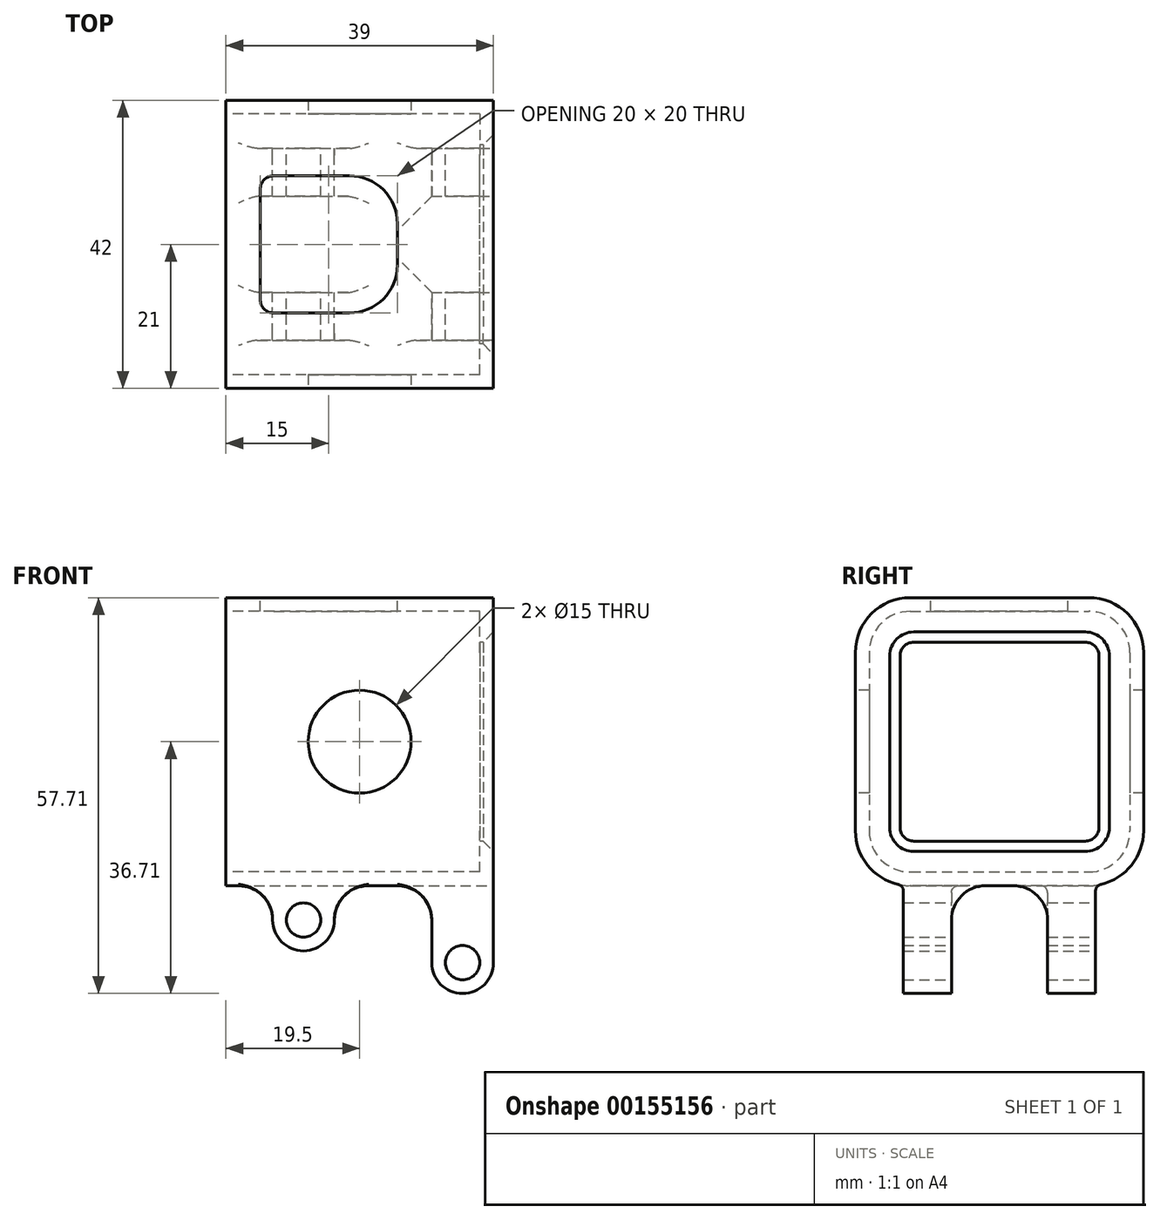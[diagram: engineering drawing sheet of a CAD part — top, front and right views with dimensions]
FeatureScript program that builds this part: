
annotation { "Feature Type Name" : "Feature", "Feature Type Description" : "" }
export const myFeature = defineFeature(function(context is Context, id is Id, definition is map)
    precondition{}
    {
        {
            var Q0;
            Q0=qCreatedBy(makeId("Right.planeOp"),FACE);
            var sketch = newSketch(context, id + "F0", { "sketchPlane" : qUnion([Q0])});
            skLineSegment(sketch, "E0.bottom", {"start": v(-13, 21) * mm, "end": v(13, 21) * mm});
            skLineSegment(sketch, "E0.top", {"start": v(-13, -21) * mm, "end": v(13, -21) * mm});
            skLineSegment(sketch, "E0.left", {"start": v(-21, 13) * mm, "end": v(-21, -13) * mm});
            skLineSegment(sketch, "E0.right", {"start": v(21, 13) * mm, "end": v(21, -13) * mm});
            skLineSegment(sketch, "E1.bottom", {"start": v(-13, 19) * mm, "end": v(13, 19) * mm});
            skLineSegment(sketch, "E1.top", {"start": v(-13, -19) * mm, "end": v(13, -19) * mm});
            skLineSegment(sketch, "E1.left", {"start": v(-19, 13) * mm, "end": v(-19, -13) * mm});
            skLineSegment(sketch, "E1.right", {"start": v(19, 13) * mm, "end": v(19, -13) * mm});
            skPoint(sketch, "E2.visualSharp", {"position": v(-19, 19) * mm});
            skArc(sketch, "E2.filletArc", {"start": v(-13, 19) * mm, "mid": v(-17.24, 17.24) * mm, "end": v(-19, 13) * mm});
            skPoint(sketch, "E3.visualSharp", {"position": v(19, 19) * mm});
            skArc(sketch, "E3.filletArc", {"start": v(19, 13) * mm, "mid": v(17.24, 17.24) * mm, "end": v(13, 19) * mm});
            skPoint(sketch, "E4.visualSharp", {"position": v(19, -19) * mm});
            skArc(sketch, "E4.filletArc", {"start": v(13, -19) * mm, "mid": v(17.24, -17.24) * mm, "end": v(19, -13) * mm});
            skPoint(sketch, "E5.visualSharp", {"position": v(-19, -19) * mm});
            skArc(sketch, "E5.filletArc", {"start": v(-19, -13) * mm, "mid": v(-17.24, -17.24) * mm, "end": v(-13, -19) * mm});
            skPoint(sketch, "E6.visualSharp", {"position": v(-21, -21) * mm});
            skArc(sketch, "E6.filletArc", {"start": v(-21, -13) * mm, "mid": v(-18.66, -18.66) * mm, "end": v(-13, -21) * mm});
            skPoint(sketch, "E7.visualSharp", {"position": v(21, -21) * mm});
            skArc(sketch, "E7.filletArc", {"start": v(13, -21) * mm, "mid": v(18.66, -18.66) * mm, "end": v(21, -13) * mm});
            skPoint(sketch, "E8.visualSharp", {"position": v(21, 21) * mm});
            skArc(sketch, "E8.filletArc", {"start": v(21, 13) * mm, "mid": v(18.66, 18.66) * mm, "end": v(13, 21) * mm});
            skPoint(sketch, "E9.visualSharp", {"position": v(-21, 21) * mm});
            skArc(sketch, "E9.filletArc", {"start": v(-13, 21) * mm, "mid": v(-18.66, 18.66) * mm, "end": v(-21, 13) * mm});
            skSolve(sketch);
        }
        {
            var Q0;
            Q0 = qSketchRegion(id + "F0", true);
            extrude(context, id + "F1", {"entities" : qUnion([Q0]), "endBound" : BoundingType.SYMMETRIC, "depth" : 37 * mm});
        }
        {
            var Q0;
            Q0=makeQuery(id+"F1.opExtrude","CAP_FACE",FACE,{"disambiguationData":[OSD([sQuery(id+"F0.wireOp",EDGE,"E0.bottom"),sQuery(id+"F0.wireOp",EDGE,"E0.top"),sQuery(id+"F0.wireOp",EDGE,"E0.left"),sQuery(id+"F0.wireOp",EDGE,"E0.right"),sQuery(id+"F0.wireOp",EDGE,"E1.bottom"),sQuery(id+"F0.wireOp",EDGE,"E1.top"),sQuery(id+"F0.wireOp",EDGE,"E1.left"),sQuery(id+"F0.wireOp",EDGE,"E1.right"),sQuery(id+"F0.wireOp",EDGE,"E2.filletArc"),sQuery(id+"F0.wireOp",EDGE,"E3.filletArc"),sQuery(id+"F0.wireOp",EDGE,"E4.filletArc"),sQuery(id+"F0.wireOp",EDGE,"E5.filletArc"),sQuery(id+"F0.wireOp",EDGE,"E6.filletArc"),sQuery(id+"F0.wireOp",EDGE,"E7.filletArc"),sQuery(id+"F0.wireOp",EDGE,"E8.filletArc"),sQuery(id+"F0.wireOp",EDGE,"E9.filletArc")])],"isStart":false});
            var sketch = newSketch(context, id + "F2", { "sketchPlane" : qUnion([Q0])});
            skLineSegment(sketch, "E10.bottom", {"start": v(-12.5, 14.5) * mm, "end": v(12.5, 14.5) * mm});
            skLineSegment(sketch, "E10.top", {"start": v(-12.5, -14.5) * mm, "end": v(12.5, -14.5) * mm});
            skLineSegment(sketch, "E10.left", {"start": v(-14.5, 12.5) * mm, "end": v(-14.5, -12.5) * mm});
            skLineSegment(sketch, "E10.right", {"start": v(14.5, 12.5) * mm, "end": v(14.5, -12.5) * mm});
            skLineSegment(sketch, "E11.bottom", {"start": v(-13, 21) * mm, "end": v(13, 21) * mm});
            skLineSegment(sketch, "E11.top", {"start": v(-13, -21) * mm, "end": v(13, -21) * mm});
            skLineSegment(sketch, "E11.left", {"start": v(-21, 13) * mm, "end": v(-21, -13) * mm});
            skLineSegment(sketch, "E11.right", {"start": v(21, 13) * mm, "end": v(21, -13) * mm});
            skPoint(sketch, "E12.visualSharp", {"position": v(-21, 21) * mm});
            skArc(sketch, "E12.filletArc", {"start": v(-13, 21) * mm, "mid": v(-18.66, 18.66) * mm, "end": v(-21, 13) * mm});
            skPoint(sketch, "E13.visualSharp", {"position": v(-21, -21) * mm});
            skArc(sketch, "E13.filletArc", {"start": v(-21, -13) * mm, "mid": v(-18.66, -18.66) * mm, "end": v(-13, -21) * mm});
            skPoint(sketch, "E14.visualSharp", {"position": v(21, -21) * mm});
            skArc(sketch, "E14.filletArc", {"start": v(13, -21) * mm, "mid": v(18.66, -18.66) * mm, "end": v(21, -13) * mm});
            skPoint(sketch, "E15.visualSharp", {"position": v(21, 21) * mm});
            skArc(sketch, "E15.filletArc", {"start": v(21, 13) * mm, "mid": v(18.66, 18.66) * mm, "end": v(13, 21) * mm});
            skPoint(sketch, "E16.visualSharp", {"position": v(-14.5, 14.5) * mm});
            skArc(sketch, "E16.filletArc", {"start": v(-12.5, 14.5) * mm, "mid": v(-13.91, 13.91) * mm, "end": v(-14.5, 12.5) * mm});
            skPoint(sketch, "E17.visualSharp", {"position": v(-14.5, -14.5) * mm});
            skArc(sketch, "E17.filletArc", {"start": v(-14.5, -12.5) * mm, "mid": v(-13.91, -13.91) * mm, "end": v(-12.5, -14.5) * mm});
            skPoint(sketch, "E18.visualSharp", {"position": v(14.5, -14.5) * mm});
            skArc(sketch, "E18.filletArc", {"start": v(12.5, -14.5) * mm, "mid": v(13.91, -13.91) * mm, "end": v(14.5, -12.5) * mm});
            skPoint(sketch, "E19.visualSharp", {"position": v(14.5, 14.5) * mm});
            skArc(sketch, "E19.filletArc", {"start": v(14.5, 12.5) * mm, "mid": v(13.91, 13.91) * mm, "end": v(12.5, 14.5) * mm});
            skSolve(sketch);
        }
        {
            var Q0;
            Q0 = qSketchRegion(id + "F2", true);
            extrude(context, id + "F3", {"entities" : qUnion([Q0]), "operationType" : NewBodyOperationType.ADD, "depth" : 2 * mm});
        }
        {
            var Q0;
            Q0=makeQuery(id+"F3.opExtrude","CAP_EDGE",EDGE,{"disambiguationData":[OSD([sQuery(id+"F2.wireOp",EDGE,"E10.bottom")])],"isStart":false});
            chamfer(context, id + "F4", {"entities" : qUnion([Q0]), "width" : 1.5 * mm, "tangentPropagation" : true});
        }
        {
            var Q0;
            Q0=makeQuery(id+"F3.boolean.opBoolean","MERGE",FACE,{"derivedFrom":[makeQuery(id+"F1.opExtrude","SWEPT_FACE",FACE,{"disambiguationData":[OSD([sQuery(id+"F0.wireOp",EDGE,"E0.bottom")])]}),makeQuery(id+"F3.opExtrude","SWEPT_FACE",FACE,{"disambiguationData":[OSD([sQuery(id+"F2.wireOp",EDGE,"E11.bottom")])]})]});
            var sketch = newSketch(context, id + "F5", { "sketchPlane" : qUnion([Q0])});
            skLineSegment(sketch, "E20.bottom", {"start": v(-11.5, 10) * mm, "end": v(-0.5, 10) * mm});
            skLineSegment(sketch, "E20.top", {"start": v(-11.5, -10) * mm, "end": v(-0.5, -10) * mm});
            skLineSegment(sketch, "E20.left", {"start": v(-13.5, 8) * mm, "end": v(-13.5, -8) * mm});
            skLineSegment(sketch, "E20.right", {"start": v(6.5, 3) * mm, "end": v(6.5, -3) * mm});
            skPoint(sketch, "E21.visualSharp", {"position": v(-13.5, 10) * mm});
            skArc(sketch, "E21.filletArc", {"start": v(-11.5, 10) * mm, "mid": v(-12.91, 9.41) * mm, "end": v(-13.5, 8) * mm});
            skPoint(sketch, "E22.visualSharp", {"position": v(-13.5, -10) * mm});
            skArc(sketch, "E22.filletArc", {"start": v(-13.5, -8) * mm, "mid": v(-12.91, -9.41) * mm, "end": v(-11.5, -10) * mm});
            skPoint(sketch, "E23.visualSharp", {"position": v(6.5, 10) * mm});
            skArc(sketch, "E23.filletArc", {"start": v(6.5, 3) * mm, "mid": v(4.45, 7.95) * mm, "end": v(-0.5, 10) * mm});
            skPoint(sketch, "E24.visualSharp", {"position": v(6.5, -10) * mm});
            skArc(sketch, "E24.filletArc", {"start": v(-0.5, -10) * mm, "mid": v(4.45, -7.95) * mm, "end": v(6.5, -3) * mm});
            skSolve(sketch);
        }
        {
            var Q0;
            Q0 = qSketchRegion(id + "F5", true);
            extrude(context, id + "F6", {"entities" : qUnion([Q0]), "operationType" : NewBodyOperationType.REMOVE, "oppositeDirection" : true, "depth" : 5 * mm});
        }
        {
            var Q0;
            Q0=qCreatedBy(makeId("Front.planeOp"),FACE);
            var sketch = newSketch(context, id + "F7", { "sketchPlane" : qUnion([Q0])});
            skCircle(sketch, "E25", {"center": v(16, -32.21) * mm, "radius": 2.5 * mm});
            skCircle(sketch, "E26", {"center": v(-7.18, -26) * mm, "radius": 2.5 * mm});
            skLineSegment(sketch, "E27", {"start": v(-7.18, -26) * mm, "end": v(16, -32.21) * mm, "construction": true});
            skArc(sketch, "E28", {"start": v(11.5, -32.21) * mm, "mid": v(16, -36.71) * mm, "end": v(20.5, -32.21) * mm});
            skArc(sketch, "E29", {"start": v(-11.68, -26) * mm, "mid": v(-7.18, -30.5) * mm, "end": v(-2.68, -26) * mm});
            skLineSegment(sketch, "E30", {"start": v(20.5, -32.21) * mm, "end": v(20.5, -20) * mm});
            skLineSegment(sketch, "E31", {"start": v(11.5, -32.21) * mm, "end": v(11.5, -20) * mm});
            skLineSegment(sketch, "E32", {"start": v(-2.68, -26) * mm, "end": v(-2.68, -20) * mm});
            skLineSegment(sketch, "E33", {"start": v(-2.68, -20) * mm, "end": v(-11.68, -20) * mm});
            skLineSegment(sketch, "E34", {"start": v(-11.68, -20) * mm, "end": v(-11.68, -26) * mm});
            skLineSegment(sketch, "E35", {"start": v(-2.68, -20) * mm, "end": v(11.5, -20) * mm, "construction": true});
            skLineSegment(sketch, "E36", {"start": v(11.5, -20) * mm, "end": v(20.5, -20) * mm});
            skPoint(sketch, "E36.endSnap0", {"position": v(4.4, -20) * mm});
            skSolve(sketch);
        }
        {
            var Q0;
            Q0 = qSketchRegion(id + "F7", true);
            extrude(context, id + "F8", {"entities" : qUnion([Q0]), "operationType" : NewBodyOperationType.ADD, "endBound" : BoundingType.SYMMETRIC, "depth" : 28 * mm});
        }
        {
            var Q0;
            Q0=makeQuery(id+"F8.boolean.opBoolean","INTERSECT",EDGE,{"derivedFrom":[makeQuery(id+"F3.boolean.opBoolean","MERGE",FACE,{"derivedFrom":[makeQuery(id+"F1.opExtrude","SWEPT_FACE",FACE,{"disambiguationData":[OSD([sQuery(id+"F0.wireOp",EDGE,"E0.top")])]}),makeQuery(id+"F3.opExtrude","SWEPT_FACE",FACE,{"disambiguationData":[OSD([sQuery(id+"F2.wireOp",EDGE,"E11.top")])]})]}),makeQuery(id+"F8.opExtrude","SWEPT_FACE",FACE,{"disambiguationData":[OSD([sQuery(id+"F7.wireOp",EDGE,"E34")])]})]});
            var Q1;
            Q1=makeQuery(id+"F8.boolean.opBoolean","INTERSECT",EDGE,{"derivedFrom":[makeQuery(id+"F3.boolean.opBoolean","MERGE",FACE,{"derivedFrom":[makeQuery(id+"F1.opExtrude","SWEPT_FACE",FACE,{"disambiguationData":[OSD([sQuery(id+"F0.wireOp",EDGE,"E0.top")])]}),makeQuery(id+"F3.opExtrude","SWEPT_FACE",FACE,{"disambiguationData":[OSD([sQuery(id+"F2.wireOp",EDGE,"E11.top")])]})]}),makeQuery(id+"F8.opExtrude","SWEPT_FACE",FACE,{"disambiguationData":[OSD([sQuery(id+"F7.wireOp",EDGE,"E32")])]})]});
            var Q2;
            Q2=makeQuery(id+"F8.boolean.opBoolean","INTERSECT",EDGE,{"derivedFrom":[makeQuery(id+"F3.boolean.opBoolean","MERGE",FACE,{"derivedFrom":[makeQuery(id+"F1.opExtrude","SWEPT_FACE",FACE,{"disambiguationData":[OSD([sQuery(id+"F0.wireOp",EDGE,"E0.top")])]}),makeQuery(id+"F3.opExtrude","SWEPT_FACE",FACE,{"disambiguationData":[OSD([sQuery(id+"F2.wireOp",EDGE,"E11.top")])]})]}),makeQuery(id+"F8.opExtrude","SWEPT_FACE",FACE,{"disambiguationData":[OSD([sQuery(id+"F7.wireOp",EDGE,"E31")])]})]});
            fillet(context, id + "F9", {"entities" : qUnion([Q0, Q1, Q2]), "radius" : 5 * mm, "tangentPropagation" : true, "allowEdgeOverflow" : false});
        }
        {
            var Q0;
            Q0=qCreatedBy(makeId("Front.planeOp"),FACE);
            var sketch = newSketch(context, id + "F10", { "sketchPlane" : qUnion([Q0])});
            skCircle(sketch, "E37", {"center": v(1, 0) * mm, "radius": 7.5 * mm});
            skSolve(sketch);
        }
        {
            var Q0;
            Q0 = qSketchRegion(id + "F10", true);
            extrude(context, id + "F11", {"entities" : qUnion([Q0]), "operationType" : NewBodyOperationType.REMOVE, "endBound" : BoundingType.SYMMETRIC, "oppositeDirection" : true, "depth" : 45 * mm});
        }
        {
            var Q0;
            Q0=makeQuery(id+"F8.boolean.opBoolean","SPLIT",FACE,{"disambiguationData":[TD([makeQuery(id+"F8.opExtrude","SWEPT_FACE",FACE,{"disambiguationData":[OSD([sQuery(id+"F7.wireOp",EDGE,"E31")])]})])],"derivedFrom":makeQuery(id+"F3.boolean.opBoolean","MERGE",FACE,{"derivedFrom":[makeQuery(id+"F1.opExtrude","SWEPT_FACE",FACE,{"disambiguationData":[OSD([sQuery(id+"F0.wireOp",EDGE,"E0.top")])]}),makeQuery(id+"F3.opExtrude","SWEPT_FACE",FACE,{"disambiguationData":[OSD([sQuery(id+"F2.wireOp",EDGE,"E11.top")])]})]})});
            var sketch = newSketch(context, id + "F12", { "sketchPlane" : qUnion([Q0])});
            skLineSegment(sketch, "E38.bottom", {"start": v(-18.5, 7) * mm, "end": v(20.5, 7) * mm});
            skLineSegment(sketch, "E38.top", {"start": v(-18.5, -7) * mm, "end": v(20.5, -7) * mm});
            skLineSegment(sketch, "E38.left", {"start": v(-18.5, 7) * mm, "end": v(-18.5, -7) * mm});
            skLineSegment(sketch, "E38.right", {"start": v(20.5, 7) * mm, "end": v(20.5, -7) * mm});
            skSolve(sketch);
        }
        {
            var Q0;
            Q0 = qSketchRegion(id + "F12", true);
            extrude(context, id + "F13", {"entities" : qUnion([Q0]), "operationType" : NewBodyOperationType.REMOVE, "depth" : 25 * mm});
        }
        {
            var Q0;
            {var subQ0=sQuery(id+"F12.wireOp",EDGE,"E38.bottom");Q0=makeQuery(id+"F13.boolean.opBoolean","COPY",EDGE,{"disambiguationData":[TD([makeQuery(id+"F8.opExtrude","SWEPT_FACE",FACE,{"disambiguationData":[OSD([sQuery(id+"F7.wireOp",EDGE,"E30")])]})])],"derivedFrom":makeQuery(id+"F13.opExtrude","CAP_EDGE",EDGE,{"disambiguationData":[OSD([subQ0])],"isStart":true})});}
            var Q1;
            {var subQ0=sQuery(id+"F12.wireOp",EDGE,"E38.top");Q1=makeQuery(id+"F13.boolean.opBoolean","COPY",EDGE,{"disambiguationData":[TD([makeQuery(id+"F8.opExtrude","SWEPT_FACE",FACE,{"disambiguationData":[OSD([sQuery(id+"F7.wireOp",EDGE,"E30")])]})])],"derivedFrom":makeQuery(id+"F13.opExtrude","CAP_EDGE",EDGE,{"disambiguationData":[OSD([subQ0])],"isStart":true})});}
            fillet(context, id + "F14", {"entities" : qUnion([Q0, Q1]), "radius" : 5 * mm, "tangentPropagation" : true, "allowEdgeOverflow" : false});
        }
        {
            var Q0;
            Q0=makeQuery(id+"F8.boolean.opBoolean","INTERSECT",EDGE,{"derivedFrom":[makeQuery(id+"F3.boolean.opBoolean","MERGE",FACE,{"derivedFrom":[makeQuery(id+"F1.opExtrude","SWEPT_FACE",FACE,{"disambiguationData":[OSD([sQuery(id+"F0.wireOp",EDGE,"E7.filletArc")])]}),makeQuery(id+"F3.opExtrude","SWEPT_FACE",FACE,{"disambiguationData":[OSD([sQuery(id+"F2.wireOp",EDGE,"E14.filletArc")])]})]}),makeQuery(id+"F8.opExtrude","CAP_FACE",FACE,{"disambiguationData":[OSD([sQuery(id+"F7.wireOp",EDGE,"E25"),sQuery(id+"F7.wireOp",EDGE,"E28"),sQuery(id+"F7.wireOp",EDGE,"E30"),sQuery(id+"F7.wireOp",EDGE,"E31"),sQuery(id+"F7.wireOp",EDGE,"E36")])],"isStart":true})]});
            var Q1;
            Q1=makeQuery(id+"F8.boolean.opBoolean","INTERSECT",EDGE,{"derivedFrom":[makeQuery(id+"F3.boolean.opBoolean","MERGE",FACE,{"derivedFrom":[makeQuery(id+"F1.opExtrude","SWEPT_FACE",FACE,{"disambiguationData":[OSD([sQuery(id+"F0.wireOp",EDGE,"E7.filletArc")])]}),makeQuery(id+"F3.opExtrude","SWEPT_FACE",FACE,{"disambiguationData":[OSD([sQuery(id+"F2.wireOp",EDGE,"E14.filletArc")])]})]}),makeQuery(id+"F8.opExtrude","CAP_FACE",FACE,{"disambiguationData":[OSD([sQuery(id+"F7.wireOp",EDGE,"E26"),sQuery(id+"F7.wireOp",EDGE,"E29"),sQuery(id+"F7.wireOp",EDGE,"E32"),sQuery(id+"F7.wireOp",EDGE,"E33"),sQuery(id+"F7.wireOp",EDGE,"E34")])],"isStart":true})]});
            var Q2;
            Q2=makeQuery(id+"F8.boolean.opBoolean","INTERSECT",EDGE,{"derivedFrom":[makeQuery(id+"F3.boolean.opBoolean","MERGE",FACE,{"derivedFrom":[makeQuery(id+"F1.opExtrude","SWEPT_FACE",FACE,{"disambiguationData":[OSD([sQuery(id+"F0.wireOp",EDGE,"E6.filletArc")])]}),makeQuery(id+"F3.opExtrude","SWEPT_FACE",FACE,{"disambiguationData":[OSD([sQuery(id+"F2.wireOp",EDGE,"E13.filletArc")])]})]}),makeQuery(id+"F8.opExtrude","CAP_FACE",FACE,{"disambiguationData":[OSD([sQuery(id+"F7.wireOp",EDGE,"E25"),sQuery(id+"F7.wireOp",EDGE,"E28"),sQuery(id+"F7.wireOp",EDGE,"E30"),sQuery(id+"F7.wireOp",EDGE,"E31"),sQuery(id+"F7.wireOp",EDGE,"E36")])],"isStart":false})]});
            var Q3;
            Q3=makeQuery(id+"F8.boolean.opBoolean","INTERSECT",EDGE,{"derivedFrom":[makeQuery(id+"F3.boolean.opBoolean","MERGE",FACE,{"derivedFrom":[makeQuery(id+"F1.opExtrude","SWEPT_FACE",FACE,{"disambiguationData":[OSD([sQuery(id+"F0.wireOp",EDGE,"E6.filletArc")])]}),makeQuery(id+"F3.opExtrude","SWEPT_FACE",FACE,{"disambiguationData":[OSD([sQuery(id+"F2.wireOp",EDGE,"E13.filletArc")])]})]}),makeQuery(id+"F8.opExtrude","CAP_FACE",FACE,{"disambiguationData":[OSD([sQuery(id+"F7.wireOp",EDGE,"E26"),sQuery(id+"F7.wireOp",EDGE,"E29"),sQuery(id+"F7.wireOp",EDGE,"E32"),sQuery(id+"F7.wireOp",EDGE,"E33"),sQuery(id+"F7.wireOp",EDGE,"E34")])],"isStart":false})]});
            var Q4;
            {var subQ0=sQuery(id+"F2.wireOp",EDGE,"E11.top");var subQ1=sQuery(id+"F0.wireOp",EDGE,"E0.top");var subQ2=sQuery(id+"F12.wireOp",EDGE,"E38.bottom");Q4=makeQuery(id+"F13.boolean.opBoolean","COPY",EDGE,{"disambiguationData":[TD([makeQuery(id+"F9.opFillet","BLEND_FACE",FACE,{"disambiguationData":[OSD([subQ1,subQ0,sQuery(id+"F7.wireOp",EDGE,"E32")])]})])],"derivedFrom":makeQuery(id+"F13.opExtrude","CAP_EDGE",EDGE,{"disambiguationData":[OSD([subQ2])],"isStart":true})});}
            var Q5;
            {var subQ0=sQuery(id+"F2.wireOp",EDGE,"E11.top");var subQ1=sQuery(id+"F0.wireOp",EDGE,"E0.top");var subQ2=sQuery(id+"F12.wireOp",EDGE,"E38.top");Q5=makeQuery(id+"F13.boolean.opBoolean","COPY",EDGE,{"disambiguationData":[TD([makeQuery(id+"F9.opFillet","BLEND_FACE",FACE,{"disambiguationData":[OSD([subQ1,subQ0,sQuery(id+"F7.wireOp",EDGE,"E32")])]})])],"derivedFrom":makeQuery(id+"F13.opExtrude","CAP_EDGE",EDGE,{"disambiguationData":[OSD([subQ2])],"isStart":true})});}
            fillet(context, id + "F15", {"entities" : qUnion([Q0, Q1, Q2, Q3, Q4, Q5]), "radius" : 1 * mm, "tangentPropagation" : true, "allowEdgeOverflow" : false});
        }
    });
